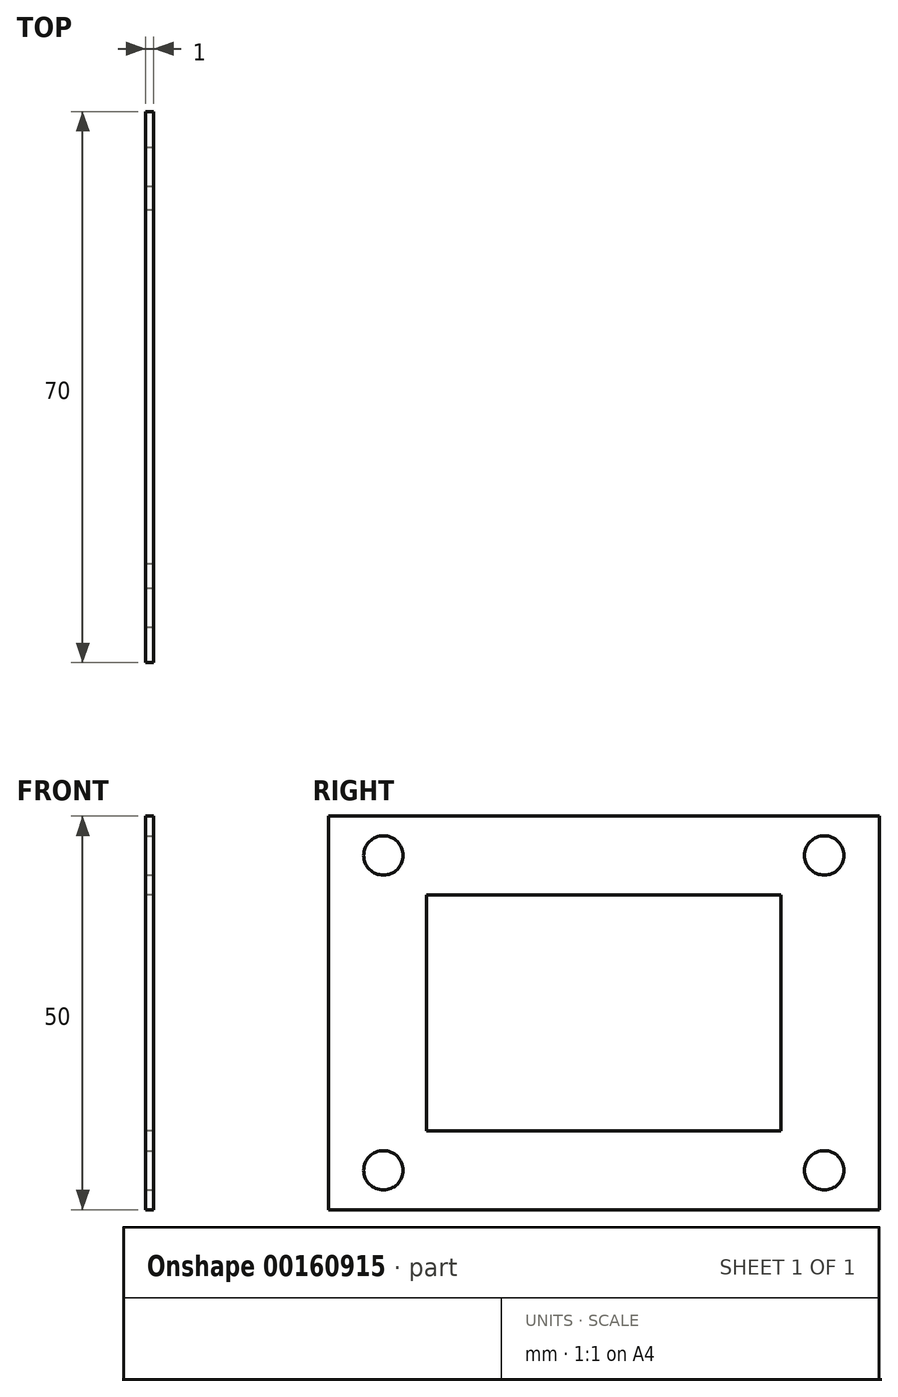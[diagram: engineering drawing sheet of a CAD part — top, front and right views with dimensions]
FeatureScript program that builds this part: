
annotation { "Feature Type Name" : "Feature", "Feature Type Description" : "" }
export const myFeature = defineFeature(function(context is Context, id is Id, definition is map)
    precondition{}
    {
        {
            var Q0;
            Q0=qCreatedBy(makeId("Right.planeOp"),FACE);
            var sketch = newSketch(context, id + "F0", { "sketchPlane" : qUnion([Q0])});
            skLineSegment(sketch, "E0.bottom", {"start": v(35, -25) * mm, "end": v(-35, -25) * mm});
            skLineSegment(sketch, "E0.top", {"start": v(35, 25) * mm, "end": v(-35, 25) * mm});
            skLineSegment(sketch, "E0.left", {"start": v(35, -25) * mm, "end": v(35, 25) * mm});
            skLineSegment(sketch, "E0.right", {"start": v(-35, -25) * mm, "end": v(-35, 25) * mm});
            skPoint(sketch, "E0.middle", {"position": v(0, 0) * mm});
            skLineSegment(sketch, "E1.bottom", {"start": v(22.5, -15) * mm, "end": v(-22.5, -15) * mm});
            skLineSegment(sketch, "E1.top", {"start": v(22.5, 15) * mm, "end": v(-22.5, 15) * mm});
            skLineSegment(sketch, "E1.left", {"start": v(22.5, -15) * mm, "end": v(22.5, 15) * mm});
            skLineSegment(sketch, "E1.right", {"start": v(-22.5, -15) * mm, "end": v(-22.5, 15) * mm});
            skSolve(sketch);
        }
        {
            var Q0;
            Q0 = qSketchRegion(id + "F0", true);
            extrude(context, id + "F1", {"entities" : qUnion([Q0]), "depth" : 0.5 * mm, "hasSecondDirection" : true, "secondDirectionOppositeDirection" : true, "secondDirectionDepth" : 0.5 * mm});
        }
        {
            var Q0;
            Q0=makeQuery(id+"F1.opExtrude","CAP_FACE",FACE,{"disambiguationData":[OSD([sQuery(id+"F0.wireOp",EDGE,"E0.bottom"),sQuery(id+"F0.wireOp",EDGE,"E0.top"),sQuery(id+"F0.wireOp",EDGE,"E0.left"),sQuery(id+"F0.wireOp",EDGE,"E0.right"),sQuery(id+"F0.wireOp",EDGE,"E1.bottom"),sQuery(id+"F0.wireOp",EDGE,"E1.top"),sQuery(id+"F0.wireOp",EDGE,"E1.left"),sQuery(id+"F0.wireOp",EDGE,"E1.right")])],"isStart":false});
            var sketch = newSketch(context, id + "F2", { "sketchPlane" : qUnion([Q0])});
            skCircle(sketch, "E2", {"center": v(-28, 20) * mm, "radius": 2.5 * mm});
            skCircle(sketch, "E3.MirrorC", {"center": v(28, 20) * mm, "radius": 2.5 * mm});
            skCircle(sketch, "E4.MirrorC", {"center": v(-28, -20) * mm, "radius": 2.5 * mm});
            skCircle(sketch, "E5.MirrorC", {"center": v(28, -20) * mm, "radius": 2.5 * mm});
            skSolve(sketch);
        }
        {
            var Q0;
            Q0 = qSketchRegion(id + "F2", true);
            extrude(context, id + "F3", {"entities" : qUnion([Q0]), "operationType" : NewBodyOperationType.REMOVE, "oppositeDirection" : true, "depth" : 2 * mm});
        }
    });
